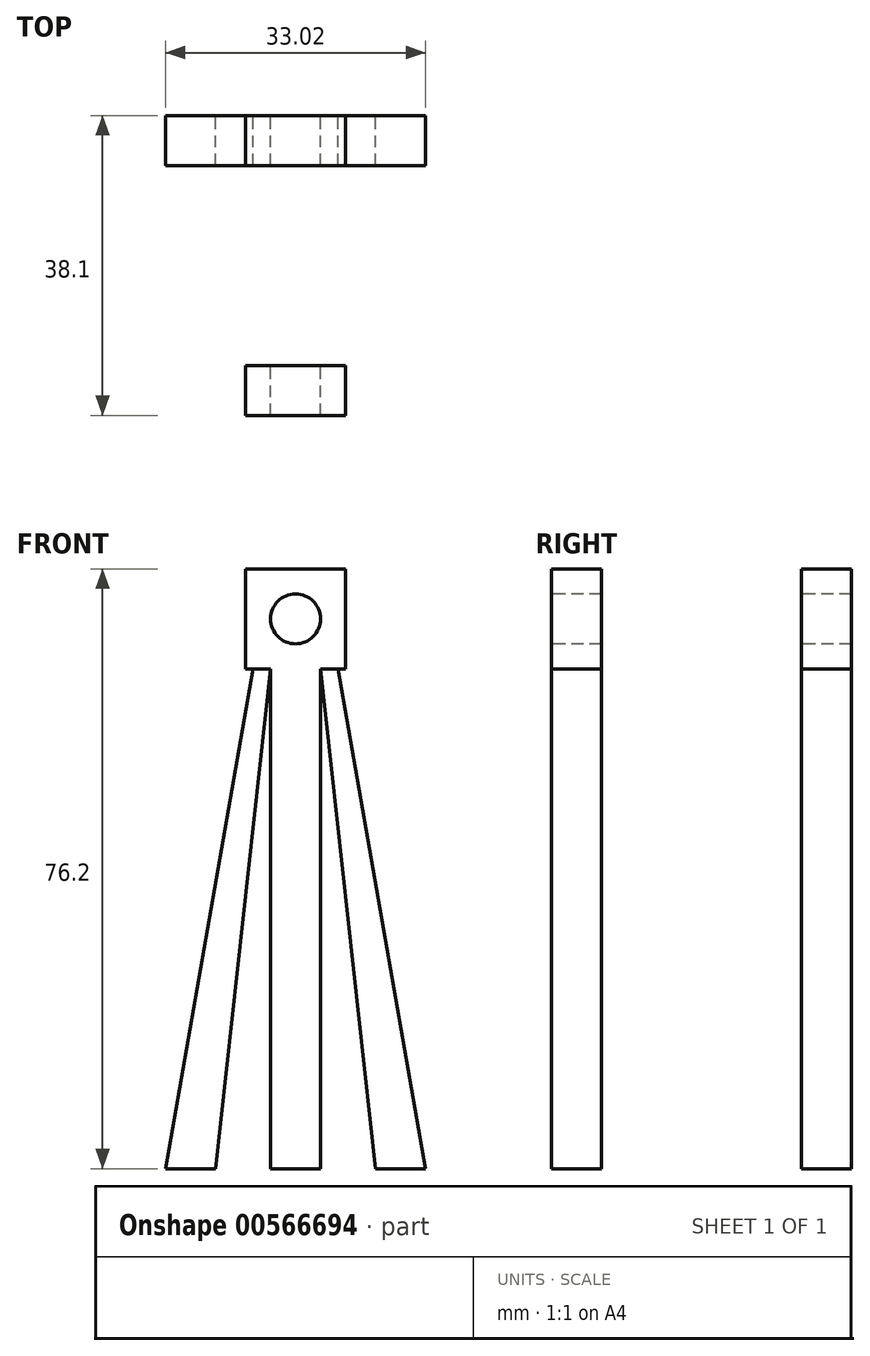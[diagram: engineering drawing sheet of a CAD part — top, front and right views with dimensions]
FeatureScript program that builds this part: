
annotation { "Feature Type Name" : "Feature", "Feature Type Description" : "" }
export const myFeature = defineFeature(function(context is Context, id is Id, definition is map)
    precondition{}
    {
        {
            var Q0;
            Q0=qCreatedBy(makeId("Front.planeOp"),FACE);
            var sketch = newSketch(context, id + "F0", { "sketchPlane" : qUnion([Q0])});
            skLineSegment(sketch, "E0", {"start": v(-3.17, 0) * mm, "end": v(-3.18, 76.2) * mm});
            skLineSegment(sketch, "E1", {"start": v(-3.18, 76.2) * mm, "end": v(3.18, 76.2) * mm});
            skLineSegment(sketch, "E2", {"start": v(3.17, 76.2) * mm, "end": v(3.17, 0) * mm});
            skLineSegment(sketch, "E3", {"start": v(3.17, 0) * mm, "end": v(-3.17, 0) * mm});
            skSolve(sketch);
        }
        {
            var Q0;
            Q0 = qSketchRegion(id + "F0", true);
            extrude(context, id + "F1", {"entities" : qUnion([Q0]), "depth" : 6.35 * mm, "offsetDistance" : 25.4 * mm});
        }
        {
            var Q0;
            Q0=qCreatedBy(makeId("Front.planeOp"),FACE);
            var sketch = newSketch(context, id + "F2", { "sketchPlane" : qUnion([Q0])});
            skPoint(sketch, "E4.0", {"position": v(-3.18, 76.2) * mm});
            skPoint(sketch, "E5.0", {"position": v(3.18, 76.2) * mm});
            skLineSegment(sketch, "E6", {"start": v(-3.18, 76.2) * mm, "end": v(-16.51, 0) * mm});
            skLineSegment(sketch, "E7", {"start": v(-16.51, 0) * mm, "end": v(-10.16, 0) * mm});
            skLineSegment(sketch, "E8", {"start": v(-10.16, 0) * mm, "end": v(-3.18, 63.5) * mm});
            skLineSegment(sketch, "E9", {"start": v(-3.18, 63.5) * mm, "end": v(-3.18, 76.2) * mm});
            skLineSegment(sketch, "E10", {"start": v(3.18, 76.2) * mm, "end": v(16.51, 0) * mm});
            skLineSegment(sketch, "E11", {"start": v(16.51, 0) * mm, "end": v(10.16, 0) * mm});
            skLineSegment(sketch, "E12", {"start": v(10.16, 0) * mm, "end": v(3.18, 63.5) * mm});
            skLineSegment(sketch, "E13", {"start": v(3.17, 63.5) * mm, "end": v(3.17, 76.2) * mm});
            skSolve(sketch);
        }
        {
            var Q0;
            Q0 = qSketchRegion(id + "F2", true);
            extrude(context, id + "F3", {"entities" : qUnion([Q0]), "operationType" : NewBodyOperationType.ADD, "depth" : 6.35 * mm, "offsetDistance" : 25.4 * mm});
        }
        {
            var Q0;
            Q0=qCreatedBy(makeId("Front.planeOp"),FACE);
            var sketch = newSketch(context, id + "F4", { "sketchPlane" : qUnion([Q0])});
            skLineSegment(sketch, "E14", {"start": v(0, 63.5) * mm, "end": v(-6.35, 63.5) * mm});
            skLineSegment(sketch, "E15", {"start": v(-6.35, 63.5) * mm, "end": v(-6.35, 76.2) * mm});
            skLineSegment(sketch, "E16.0", {"start": v(-3.18, 76.2) * mm, "end": v(3.18, 76.2) * mm});
            skLineSegment(sketch, "E17", {"start": v(-6.35, 76.2) * mm, "end": v(6.35, 76.2) * mm});
            skLineSegment(sketch, "E18", {"start": v(6.35, 76.2) * mm, "end": v(6.35, 63.5) * mm});
            skLineSegment(sketch, "E19", {"start": v(6.35, 63.5) * mm, "end": v(0, 63.5) * mm});
            skSolve(sketch);
        }
        {
            var Q0;
            Q0 = qSketchRegion(id + "F4", true);
            extrude(context, id + "F5", {"entities" : qUnion([Q0]), "operationType" : NewBodyOperationType.ADD, "depth" : 6.35 * mm, "offsetDistance" : 25.4 * mm});
        }
        {
            var Q0;
            Q0=makeQuery(id+"F5.boolean.opBoolean","MERGE",FACE,{"derivedFrom":[makeQuery(id+"F3.boolean.opBoolean","MERGE",FACE,{"derivedFrom":[makeQuery(id+"F1.opExtrude","CAP_FACE",FACE,{"disambiguationData":[OSD([sQuery(id+"F0.wireOp",EDGE,"E0"),sQuery(id+"F0.wireOp",EDGE,"E1"),sQuery(id+"F0.wireOp",EDGE,"E2"),sQuery(id+"F0.wireOp",EDGE,"E3")])],"isStart":false}),makeQuery(id+"F3.opExtrude","CAP_FACE",FACE,{"disambiguationData":[OSD([sQuery(id+"F2.wireOp",EDGE,"E6"),sQuery(id+"F2.wireOp",EDGE,"E7"),sQuery(id+"F2.wireOp",EDGE,"E8"),sQuery(id+"F2.wireOp",EDGE,"E9")])],"isStart":false}),makeQuery(id+"F3.opExtrude","CAP_FACE",FACE,{"disambiguationData":[OSD([sQuery(id+"F2.wireOp",EDGE,"E10"),sQuery(id+"F2.wireOp",EDGE,"E11"),sQuery(id+"F2.wireOp",EDGE,"E12"),sQuery(id+"F2.wireOp",EDGE,"E13")])],"isStart":false})]}),makeQuery(id+"F5.opExtrude","CAP_FACE",FACE,{"disambiguationData":[OSD([sQuery(id+"F4.wireOp",EDGE,"E14"),sQuery(id+"F4.wireOp",EDGE,"E15"),sQuery(id+"F4.wireOp",EDGE,"E17"),sQuery(id+"F4.wireOp",EDGE,"E18"),sQuery(id+"F4.wireOp",EDGE,"E19")])],"isStart":false})]});
            var sketch = newSketch(context, id + "F6", { "sketchPlane" : qUnion([Q0])});
            skCircle(sketch, "E20", {"center": v(0, 69.85) * mm, "radius": 3.18 * mm});
            skSolve(sketch);
        }
        {
            var Q0;
            Q0 = qSketchRegion(id + "F6", true);
            extrude(context, id + "F7", {"entities" : qUnion([Q0]), "operationType" : NewBodyOperationType.REMOVE, "oppositeDirection" : true, "depth" : 25.4 * mm, "offsetDistance" : 25.4 * mm});
        }
        {
            var Q0;
            Q0=qCreatedBy(makeId("Top.planeOp"),FACE);
            var sketch = newSketch(context, id + "F8", { "sketchPlane" : qUnion([Q0])});
            skLineSegment(sketch, "E21.bottom", {"start": v(-3.18, -38.1) * mm, "end": v(3.17, -38.1) * mm});
            skLineSegment(sketch, "E21.top", {"start": v(-3.18, -31.75) * mm, "end": v(3.17, -31.75) * mm});
            skLineSegment(sketch, "E21.left", {"start": v(-3.18, -38.1) * mm, "end": v(-3.18, -31.75) * mm});
            skLineSegment(sketch, "E21.right", {"start": v(3.17, -38.1) * mm, "end": v(3.17, -31.75) * mm});
            skSolve(sketch);
        }
        {
            var Q0;
            Q0 = qSketchRegion(id + "F8", true);
            extrude(context, id + "F9", {"entities" : qUnion([Q0]), "depth" : 76.2 * mm, "offsetDistance" : 25.4 * mm});
        }
        {
            var Q0;
            Q0=makeQuery(id+"F9.opExtrude","SWEPT_FACE",FACE,{"disambiguationData":[OSD([sQuery(id+"F8.wireOp",EDGE,"E21.bottom")])]});
            var sketch = newSketch(context, id + "F10", { "sketchPlane" : qUnion([Q0])});
            skLineSegment(sketch, "E22.0", {"start": v(-6.35, 76.2) * mm, "end": v(6.35, 76.2) * mm});
            skLineSegment(sketch, "E23.0", {"start": v(-6.35, 63.5) * mm, "end": v(-6.35, 76.2) * mm});
            skLineSegment(sketch, "E24.0", {"start": v(6.35, 76.2) * mm, "end": v(6.35, 63.5) * mm});
            skLineSegment(sketch, "E25", {"start": v(6.35, 63.5) * mm, "end": v(-6.35, 63.5) * mm});
            skCircle(sketch, "E26", {"center": v(0, 69.85) * mm, "radius": 3.18 * mm});
            skSolve(sketch);
        }
        {
            var Q0;
            Q0 = qSketchRegion(id + "F10", true);
            extrude(context, id + "F11", {"entities" : qUnion([Q0]), "operationType" : NewBodyOperationType.ADD, "oppositeDirection" : true, "depth" : 6.35 * mm, "offsetDistance" : 25.4 * mm});
        }
        {
            var Q0;
            Q0=makeQuery(id+"F11.boolean.opBoolean","MERGE",FACE,{"derivedFrom":[makeQuery(id+"F9.opExtrude","SWEPT_FACE",FACE,{"disambiguationData":[OSD([sQuery(id+"F8.wireOp",EDGE,"E21.bottom")])]}),makeQuery(id+"F11.opExtrude","CAP_FACE",FACE,{"disambiguationData":[OSD([sQuery(id+"F10.wireOp",EDGE,"E23.0"),sQuery(id+"F10.wireOp",EDGE,"E24.0"),sQuery(id+"F10.wireOp",EDGE,"E22.0"),sQuery(id+"F10.wireOp",EDGE,"E25"),sQuery(id+"F10.wireOp",EDGE,"E26")])],"isStart":true})]});
            var sketch = newSketch(context, id + "F12", { "sketchPlane" : qUnion([Q0])});
            skCircle(sketch, "E27", {"center": v(0, 69.85) * mm, "radius": 3.18 * mm});
            skSolve(sketch);
        }
        {
            var Q0;
            Q0 = qSketchRegion(id + "F12", true);
            extrude(context, id + "F13", {"entities" : qUnion([Q0]), "operationType" : NewBodyOperationType.REMOVE, "oppositeDirection" : true, "depth" : 25.4 * mm, "offsetDistance" : 25.4 * mm});
        }
    });
